# Revit family: 205_SIBOL-100-_-300
name_source: partatom
category: Duct Accessories
units: mm (PartAtom-declared; Revit-internal decimal feet)

## family parameters
Always vertical = Yes
Cut with Voids When Loaded = No
Part Type = Breaks Into
Round Connector Dimension = Use Diameter
Shared = No
Work Plane-Based = No

## types (16) — shared parameters
Description = CIRCULAR SILENCER WITH CORE
L1 = 8 mm  [stored 0.0262467 ft]
L2 = 284 mm  [stored 0.931759 ft]
LL = 150 mm  [stored 0.492126 ft]
Manufacturer = Alnor
QmdConnectorList = 201;D;202;D
URL = http://www.ventilation-alnor.co.uk
magiPartTypeId = 205
magiProductFamilyId = SIBOL-100-*-300

## per-type parameters (varying)
| type | CD1 | CD2 | D | H2D | L2D | R | W2D | magiProductId |
| SIBOL-100-200-300 | 200 mm  [stored 0.656168 ft] | 201 mm  [stored 0.659449 ft] | 200 mm | 400 mm  [stored 1.31234 ft] | 300 mm | 100 mm  [stored 0.328084 ft] | 400 mm  [stored 1.31234 ft] | SIBOL-100-200-300 |
| SIBOL-100-1000-300 | 625 mm | 626 mm | 1000 mm | 1200 mm | 900 mm | 500 mm | 1200 mm | SIBOL-100-1000-300 |
| SIBOL-100-900-300 | 625 mm | 626 mm | 900 mm | 1100 mm | 900 mm | 450 mm | 1100 mm | SIBOL-100-900-300 |
| SIBOL-100-800-300 | 560 mm | 561 mm | 800 mm | 1000 mm | 800 mm | 400 mm  [stored 1.31234 ft] | 1000 mm | SIBOL-100-800-300 |
| SIBOL-100-710-300 | 450 mm | 451 mm | 710 mm | 910 mm | 710 mm | 355 mm | 910 mm | SIBOL-100-710-300 |
| SIBOL-100-630-300 | 400 mm  [stored 1.31234 ft] | 401 mm | 630 mm | 830 mm | 630 mm | 315 mm | 830 mm | SIBOL-100-630-300 |
| SIBOL-100-560-300 | 400 mm  [stored 1.31234 ft] | 401 mm | 560 mm | 760 mm | 560 mm | 280 mm | 760 mm | SIBOL-100-560-300 |
| SIBOL-100-500-300 | 355 mm | 356 mm | 500 mm | 700 mm | 1000 mm | 250 mm | 700 mm | SIBOL-100-500-300 |
| SIBOL-100-450-300 | 315 mm | 316 mm | 450 mm | 650 mm | 4100 mm | 225 mm | 650 mm | SIBOL-100-450-300 |
| SIBOL-100-400-300 | 300 mm | 301 mm  [stored 0.987533 ft] | 400 mm | 600 mm | 400 mm  [stored 1.31234 ft] | 200 mm  [stored 0.656168 ft] | 600 mm | SIBOL-100-400-300 |
| SIBOL-100-355-300 | 280 mm | 281 mm | 355 mm | 555 mm | 355 mm | 178 mm | 555 mm | SIBOL-100-355-300 |
| SIBOL-100-315-315 | 250 mm | 251 mm | 315 mm | 515 mm | 315 mm | 158 mm | 515 mm | SIBOL-100-315-300 |
| SIBOL-100-300-300 | 250 mm | 251 mm | 300 mm | 500 mm | 300 mm | 150 mm  [stored 0.492126 ft] | 500 mm | SIBOL-100-300-300 |
| SIBOL-100-280-300 | 250 mm | 251 mm | 280 mm | 480 mm | 300 mm | 140 mm  [stored 0.459318 ft] | 480 mm | SIBOL-100-280-300 |
| SIBOL-100-250-300 | 225 mm | 226 mm | 250 mm | 450 mm | 300 mm | 125 mm | 450 mm | SIBOL-100-250-300 |
| SIBOL-100-224-300 | 225 mm | 226 mm | 224 mm | 424 mm | 300 mm | 112 mm | 424 mm | SIBOL-100-224-300 |

note: column(s) folded — value = type name in every type: MC Product Code

note: [stored X ft] marks values corroborated as IEEE doubles in the binary element streams (Revit-internal decimal feet)

## geometry (parser evidence)
native form markers: Blend x4, Sweep x1
no freeform markers — native parametric forms only
